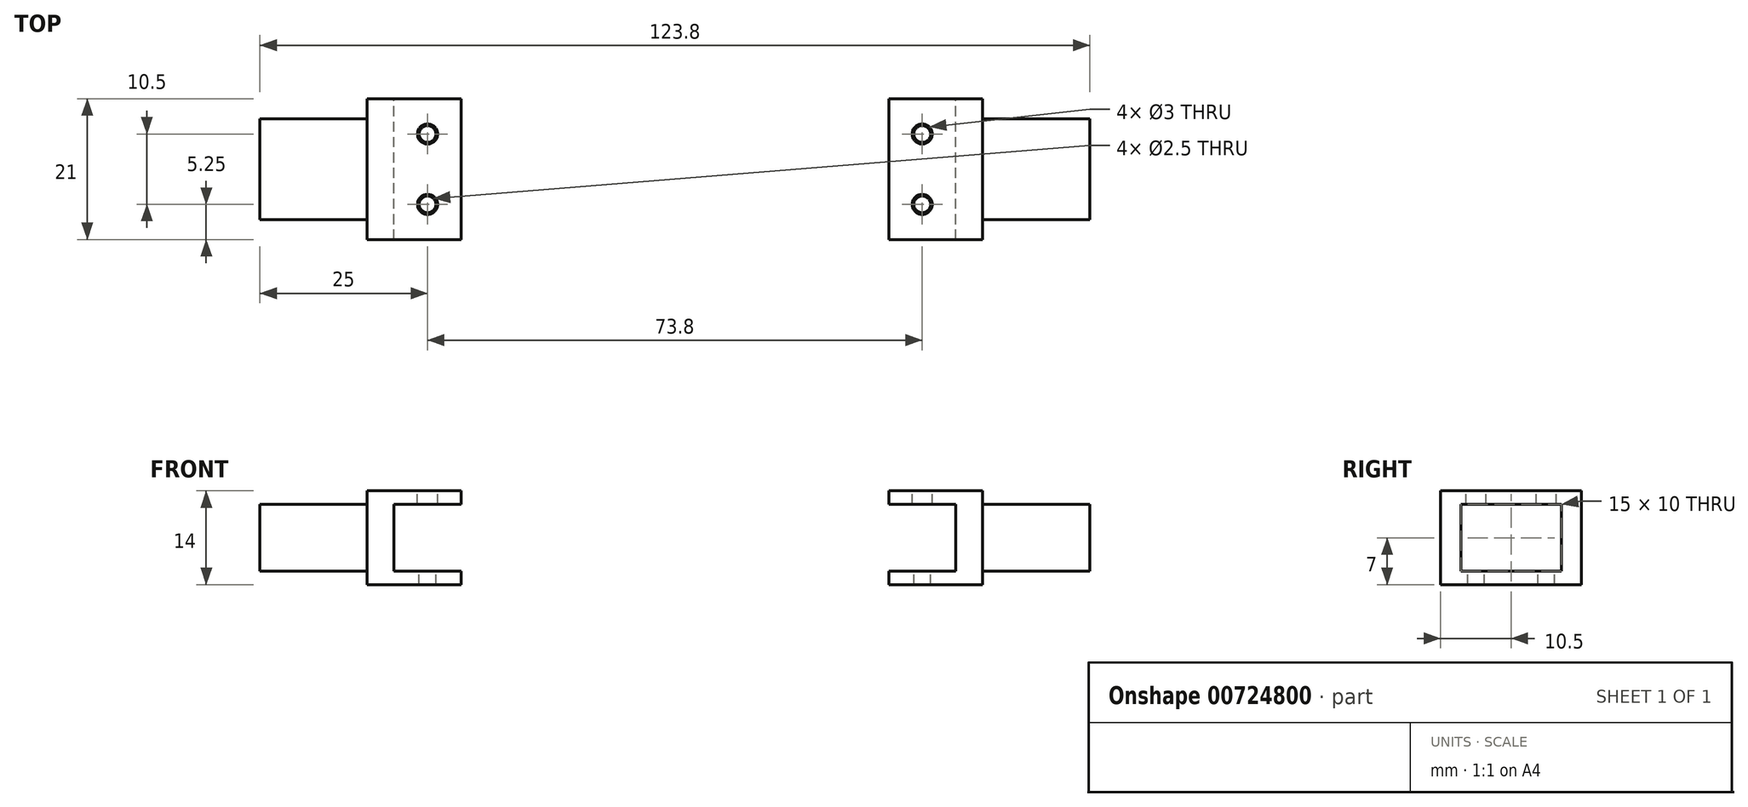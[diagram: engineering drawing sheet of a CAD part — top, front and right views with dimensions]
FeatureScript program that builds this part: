
annotation { "Feature Type Name" : "Feature", "Feature Type Description" : "" }
export const myFeature = defineFeature(function(context is Context, id is Id, definition is map)
    precondition{}
    {
        {
            var Q0;
            Q0=qCreatedBy(makeId("Front.planeOp"),FACE);
            var sketch = newSketch(context, id + "F0", { "sketchPlane" : qUnion([Q0])});
            skLineSegment(sketch, "E0", {"start": v(-31.9, 0) * mm, "end": v(-45.9, 0) * mm});
            skLineSegment(sketch, "E1", {"start": v(-45.9, 0) * mm, "end": v(-45.9, 2) * mm});
            skLineSegment(sketch, "E2", {"start": v(-45.9, 2) * mm, "end": v(-61.9, 2) * mm});
            skLineSegment(sketch, "E3", {"start": v(-61.9, 2) * mm, "end": v(-61.9, 12) * mm});
            skLineSegment(sketch, "E4", {"start": v(-61.9, 12) * mm, "end": v(-45.9, 12) * mm});
            skLineSegment(sketch, "E5", {"start": v(-45.9, 12) * mm, "end": v(-45.9, 14) * mm});
            skLineSegment(sketch, "E6", {"start": v(-45.9, 14) * mm, "end": v(-31.9, 14) * mm});
            skLineSegment(sketch, "E7", {"start": v(-31.9, 14) * mm, "end": v(-31.9, 12) * mm});
            skLineSegment(sketch, "E8", {"start": v(-31.9, 12) * mm, "end": v(-41.9, 12) * mm});
            skLineSegment(sketch, "E9", {"start": v(-41.9, 12) * mm, "end": v(-41.9, 2) * mm});
            skLineSegment(sketch, "E10", {"start": v(-41.9, 2) * mm, "end": v(-31.9, 2) * mm});
            skLineSegment(sketch, "E11", {"start": v(-31.9, 2) * mm, "end": v(-31.9, 0) * mm});
            skLineSegment(sketch, "E12", {"start": v(-45.9, 2) * mm, "end": v(-45.9, 12) * mm, "construction": true});
            skSolve(sketch);
        }
        {
            var Q0;
            Q0=makeQuery(id+"F0.imprint","IMPRINT",FACE,{"disambiguationData":[TD([[makeQuery(id+"F0.imprint","IMPRINT",EDGE,{"derivedFrom":sQuery(id+"F0.wireOp",EDGE,"E0")}),-1.0]])]});
            extrude(context, id + "F1", {"entities" : qUnion([Q0]), "depth" : 15 * mm, "offsetDistance" : 25 * mm});
        }
        {
            var Q0;
            Q0=makeQuery(id+"F1.opExtrude","CAP_FACE",FACE,{"disambiguationData":[OSD([sQuery(id+"F0.wireOp",EDGE,"E0"),sQuery(id+"F0.wireOp",EDGE,"E1"),sQuery(id+"F0.wireOp",EDGE,"E2"),sQuery(id+"F0.wireOp",EDGE,"E3"),sQuery(id+"F0.wireOp",EDGE,"E4"),sQuery(id+"F0.wireOp",EDGE,"E5"),sQuery(id+"F0.wireOp",EDGE,"E6"),sQuery(id+"F0.wireOp",EDGE,"E7"),sQuery(id+"F0.wireOp",EDGE,"E8"),sQuery(id+"F0.wireOp",EDGE,"E9"),sQuery(id+"F0.wireOp",EDGE,"E10"),sQuery(id+"F0.wireOp",EDGE,"E11")])],"isStart":false});
            var sketch = newSketch(context, id + "F2", { "sketchPlane" : qUnion([Q0])});
            skLineSegment(sketch, "E13", {"start": v(-45.9, 12) * mm, "end": v(-45.9, 2) * mm});
            skSolve(sketch);
        }
        {
            var Q0;
            Q0=makeQuery(id+"F2.imprint","IMPRINT",FACE,{"disambiguationData":[TD([[makeQuery(id+"F2.imprint","IMPRINT",EDGE,{"derivedFrom":sQuery(id+"F2.wireOp",EDGE,"E13")}),1.0]])]});
            extrude(context, id + "F3", {"entities" : qUnion([Q0]), "operationType" : NewBodyOperationType.ADD, "depth" : 3 * mm, "offsetDistance" : 25 * mm});
        }
        {
            var Q0;
            Q0=makeQuery(id+"F1.opExtrude","CAP_FACE",FACE,{"disambiguationData":[OSD([sQuery(id+"F0.wireOp",EDGE,"E0"),sQuery(id+"F0.wireOp",EDGE,"E1"),sQuery(id+"F0.wireOp",EDGE,"E2"),sQuery(id+"F0.wireOp",EDGE,"E3"),sQuery(id+"F0.wireOp",EDGE,"E4"),sQuery(id+"F0.wireOp",EDGE,"E5"),sQuery(id+"F0.wireOp",EDGE,"E6"),sQuery(id+"F0.wireOp",EDGE,"E7"),sQuery(id+"F0.wireOp",EDGE,"E8"),sQuery(id+"F0.wireOp",EDGE,"E9"),sQuery(id+"F0.wireOp",EDGE,"E10"),sQuery(id+"F0.wireOp",EDGE,"E11")])],"isStart":true});
            var sketch = newSketch(context, id + "F4", { "sketchPlane" : qUnion([Q0])});
            skLineSegment(sketch, "E14", {"start": v(45.9, 12) * mm, "end": v(45.9, 2) * mm});
            skSolve(sketch);
        }
        {
            var Q0;
            Q0=makeQuery(id+"F4.imprint","IMPRINT",FACE,{"disambiguationData":[TD([[makeQuery(id+"F4.imprint","IMPRINT",EDGE,{"derivedFrom":sQuery(id+"F4.wireOp",EDGE,"E14")}),-1.0]])]});
            extrude(context, id + "F5", {"entities" : qUnion([Q0]), "operationType" : NewBodyOperationType.ADD, "depth" : 3 * mm, "offsetDistance" : 25 * mm});
        }
        {
            var Q0;
            {var subQ0=sQuery(id+"F0.wireOp",EDGE,"E6");Q0=makeQuery(id+"F5.boolean.opBoolean","MERGE",FACE,{"derivedFrom":[makeQuery(id+"F3.boolean.opBoolean","MERGE",FACE,{"derivedFrom":[makeQuery(id+"F1.opExtrude","SWEPT_FACE",FACE,{"disambiguationData":[OSD([subQ0])]}),makeQuery(id+"F3.opExtrude","SWEPT_FACE",FACE,{"disambiguationData":[OSD([subQ0])]})]}),makeQuery(id+"F5.opExtrude","SWEPT_FACE",FACE,{"disambiguationData":[OSD([subQ0])]})]});}
            var sketch = newSketch(context, id + "F6", { "sketchPlane" : qUnion([Q0])});
            skLineSegment(sketch, "E15", {"start": v(-45.9, 3) * mm, "end": v(-31.9, 3) * mm});
            skLineSegment(sketch, "E16", {"start": v(-31.9, 3) * mm, "end": v(-31.9, -18) * mm});
            skLineSegment(sketch, "E17", {"start": v(-31.9, -18) * mm, "end": v(-45.9, -18) * mm});
            skLineSegment(sketch, "E18", {"start": v(-45.9, -18) * mm, "end": v(-45.9, 3) * mm});
            skLineSegment(sketch, "E19", {"start": v(-31.9, -7.5) * mm, "end": v(-45.9, -7.5) * mm, "construction": true});
            skLineSegment(sketch, "E20", {"start": v(-36.9, -7.5) * mm, "end": v(-36.9, 3) * mm});
            skLineSegment(sketch, "E21", {"start": v(-36.9, -7.5) * mm, "end": v(-36.9, -18) * mm});
            skPoint(sketch, "E22", {"position": v(-36.9, -2.25) * mm});
            skPoint(sketch, "E23", {"position": v(-36.9, -12.75) * mm});
            skSolve(sketch);
        }
        {
            var Q0;
            Q0=sQuery(id+"F6.wireOp",VERTEX,"E22");
            var Q1;
            Q1=sQuery(id+"F6.wireOp",VERTEX,"E23");
            var Q2;
            Q2=makeQuery(id+"F1.opExtrude","SWEPT_BODY",BODY,{"disambiguationData":[OSD([sQuery(id+"F0.wireOp",EDGE,"E0"),sQuery(id+"F0.wireOp",EDGE,"E1"),sQuery(id+"F0.wireOp",EDGE,"E2"),sQuery(id+"F0.wireOp",EDGE,"E3"),sQuery(id+"F0.wireOp",EDGE,"E4"),sQuery(id+"F0.wireOp",EDGE,"E5"),sQuery(id+"F0.wireOp",EDGE,"E6"),sQuery(id+"F0.wireOp",EDGE,"E7"),sQuery(id+"F0.wireOp",EDGE,"E8"),sQuery(id+"F0.wireOp",EDGE,"E9"),sQuery(id+"F0.wireOp",EDGE,"E10"),sQuery(id+"F0.wireOp",EDGE,"E11")])]});
            hole(context, id + "F7", {"style" : HoleStyle.C_BORE, "endStyle" : HoleEndStyle.THROUGH, "holeDiameter" : 2.5 * mm, "cBoreDiameter" : 3 * mm, "cBoreDepth" : 10 * mm, "majorDiameter" : 5 * mm, "isTappedThrough" : true, "tappedDepth" : 12 * mm, "tapClearance" : 3, "locations" : qUnion([Q0, Q1]), "scope" : qUnion([Q2])});
        }
        {
            var Q0;
            Q0=makeQuery(id+"F1.opExtrude","SWEPT_BODY",BODY,{"disambiguationData":[OSD([sQuery(id+"F0.wireOp",EDGE,"E0"),sQuery(id+"F0.wireOp",EDGE,"E1"),sQuery(id+"F0.wireOp",EDGE,"E2"),sQuery(id+"F0.wireOp",EDGE,"E3"),sQuery(id+"F0.wireOp",EDGE,"E4"),sQuery(id+"F0.wireOp",EDGE,"E5"),sQuery(id+"F0.wireOp",EDGE,"E6"),sQuery(id+"F0.wireOp",EDGE,"E7"),sQuery(id+"F0.wireOp",EDGE,"E8"),sQuery(id+"F0.wireOp",EDGE,"E9"),sQuery(id+"F0.wireOp",EDGE,"E10"),sQuery(id+"F0.wireOp",EDGE,"E11")])]});
            var Q1;
            Q1=qCreatedBy(makeId("Right.planeOp"),FACE);
            mirror(context, id + "F8", {"entities" : qUnion([Q0]), "mirrorPlane" : qUnion([Q1])});
        }
    });
